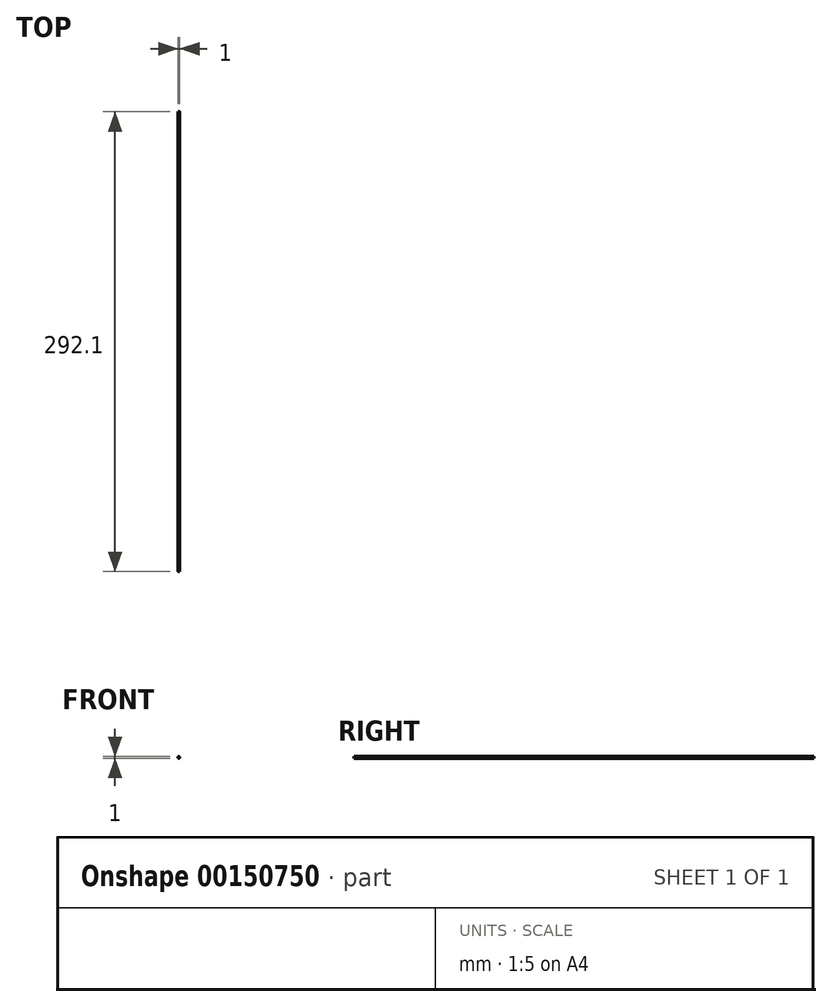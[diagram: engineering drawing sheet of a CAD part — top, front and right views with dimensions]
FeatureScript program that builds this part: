
annotation { "Feature Type Name" : "Feature", "Feature Type Description" : "" }
export const myFeature = defineFeature(function(context is Context, id is Id, definition is map)
    precondition{}
    {
        {
            var Q0;
            Q0=qCreatedBy(makeId("Front.planeOp"),FACE);
            var sketch = newSketch(context, id + "F0", { "sketchPlane" : qUnion([Q0])});
            skCircle(sketch, "E0", {"center": v(0, 0) * mm, "radius": 0.5 * mm});
            skSolve(sketch);
        }
        {
            var Q0;
            Q0=makeQuery(id+"F0.imprint","IMPRINT",FACE,{"disambiguationData":[TD([[makeQuery(id+"F0.imprint","IMPRINT",EDGE,{"derivedFrom":sQuery(id+"F0.wireOp",EDGE,"E0")}),1.0]])]});
            extrude(context, id + "F1", {"entities" : qUnion([Q0]), "depth" : 292.1 * mm});
        }
    });
